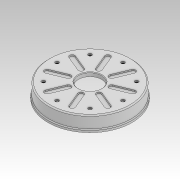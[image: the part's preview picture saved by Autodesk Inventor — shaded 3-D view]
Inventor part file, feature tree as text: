
AUTODESK INVENTOR PART (.ipt)
format: ipt  version: 2020 (Build 240168000, 168)  size: 1,567,744 bytes
history: native  units: mm
features: other x11, extrude x6, sketch x6, pattern_circular x4, chamfer x2, fillet x2, revolve x1, imported_body x1
ambient origin geometry x8: Origin, YZ Plane, XZ Plane, XY Plane, X Axis, Y Axis, Z Axis, Center Point
bodies: Solid1 (feature_tree)
feature tree (33):
  other  "HD_mastersketch.ipt"
  other  "Blocks"
  revolve  "Revolution1"  [1 undecoded]
  extrude  "Extrusion1"  Depth=4.0mm TaperAngle=0.0deg
  extrude  "Extrusion3"  Depth=1.7mm
  pattern_circular  "Circular Pattern1"  Count=73 Angle=360.0deg
  chamfer  "Chamfer1"  Distance=3.2mm
  extrude  "Extrusion2"  Depth=1.0mm
  fillet  "Fillet1"  Radius=4.0mm
  pattern_circular  "Circular Pattern2"  Angle=45.0deg  [1 undecoded]
  extrude  "Extrusion5"  Depth=10.0mm TaperAngle=0.0deg
  fillet  "Fillet2"  Radius=0.5mm
  pattern_circular  "Circular Pattern3"  Count=68 Angle=360.0deg
  extrude  "Extrusion6"  Depth=1.0mm
  chamfer  "Chamfer2"  Distance=22.5mm
  pattern_circular  "Circular Pattern4"  [2 undecoded]
  extrude  "Extrusion7"  Depth=1.0mm TaperAngle=0.0deg
  other  "608 bearing"
  other  "Belt"
  other  "Rotor"
  imported_body  "Base"
  sketch  "Sketch5"  dims[d0=10.0mm d24=7.0mm d25=22.0mm d26=8.0mm]
  sketch  "Sketch6"  dims[d1=90.0deg d4=4.0mm d5=0.0mm]
  sketch  "Sketch7"  dims[d6=80.0mm d7=360.0deg d9=1.7mm]
  other  "M3NutDepth_bot"
  other  "BeltCutDepth_bot"
  other  "M3NutDepth_top"
  other  "BeltCutDepth_top"
  sketch  "Sketch10"  dims[d11=1.25mm]
  sketch  "Sketch11"  dims[d12=4.0mm d13=0.0mm]
  sketch  "Sketch12"  dims[d14=0.5mm d15=730.0mm d16=360.0deg d18=3.2mm d19=5.7mm d20=4.0mm d21=0.0mm d34=0.5mm d35=2.0mm d36=45.0deg d37=0.8mm d38=1.8mm d39=8.726646mm d40=0.523599mm d41=0.523599mm d42=0.523599mm d43=0.523599mm d44=0.523599mm d45=2.792527mm d46=0.523599mm d47=68.0mm d48=70.740362mm d49=1.780032mm d50=9.749343mm d51=7.969311mm d52=6.189278mm d53=4.409246mm d54=2.629213mm d55=0.523599mm d56=0.523599mm d57=0.523599mm d58=0.523599mm d59=0.523599mm d60=11.529376mm d61=13.309408mm d62=15.089441mm d63=16.869473mm d64=18.649506mm d65=0.523599mm d66=0.523599mm d67=20.429538mm d68=22.209571mm d69=0.243598mm d70=72.932651mm d71=10.0mm d72=0.0mm d73=0.5mm d74=680.0mm d75=360.0deg d78=15.0mm d79=22.5mm d80=2.0mm d81=1.0mm d82=0.0mm d83=0.3mm d84=1.0mm d85=45.0deg d86=80.0mm d87=360.0deg d89=10.0mm d90=0.0mm d91=1.0mm d92=0.5mm d93=0.872665mm d94=0.5mm d95=0.872665mm]
  other  "608 bearing:1"
  other  "608 bearing:2"
note: 4 required parameter values undecoded (feature->parameter linkage not recoverable at this tier; creation-order binding heuristic only, values carry confidence <= 0.55)